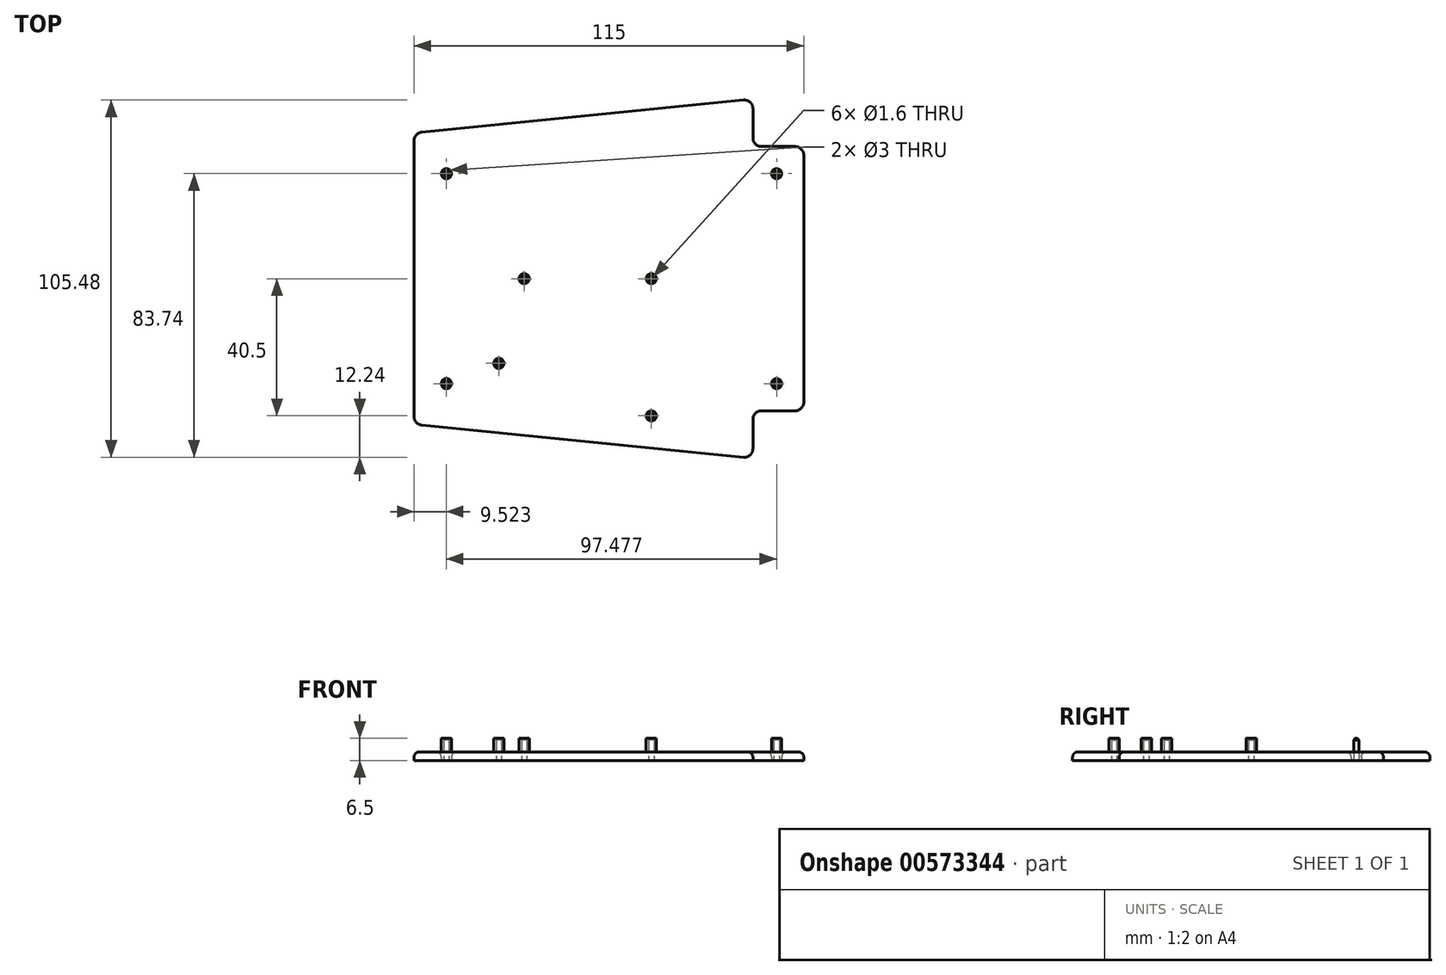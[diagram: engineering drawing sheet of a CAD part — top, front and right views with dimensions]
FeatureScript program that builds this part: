
annotation { "Feature Type Name" : "Feature", "Feature Type Description" : "" }
export const myFeature = defineFeature(function(context is Context, id is Id, definition is map)
    precondition{}
    {
        {
            var Q0;
            Q0=qCreatedBy(makeId("Top.planeOp"),FACE);
            var sketch = newSketch(context, id + "F0", { "sketchPlane" : qUnion([Q0])});
            skLineSegment(sketch, "E0", {"start": v(100, 0) * mm, "end": v(115, 0) * mm, "construction": true});
            skLineSegment(sketch, "E1", {"start": v(115, 0) * mm, "end": v(125, 0) * mm, "construction": true});
            skLineSegment(sketch, "E2", {"start": v(125, 0) * mm, "end": v(125, -55.5) * mm, "construction": true});
            skLineSegment(sketch, "E3.MirrorCS", {"start": v(125, 0) * mm, "end": v(125, 55.5) * mm, "construction": true});
            skLineSegment(sketch, "E4", {"start": v(100, 0) * mm, "end": v(100, -39) * mm, "construction": true});
            skLineSegment(sketch, "E5.MirrorCS", {"start": v(100, 0) * mm, "end": v(100, 39) * mm, "construction": true});
            skLineSegment(sketch, "E6", {"start": v(115, 0) * mm, "end": v(115, -39) * mm, "construction": true});
            skLineSegment(sketch, "E7.MirrorCS", {"start": v(115, 0) * mm, "end": v(115, 39) * mm, "construction": true});
            skLineSegment(sketch, "E8", {"start": v(100, 39) * mm, "end": v(115, 39) * mm});
            skLineSegment(sketch, "E9", {"start": v(115, 39) * mm, "end": v(115, -39) * mm});
            skLineSegment(sketch, "E10", {"start": v(115, -39) * mm, "end": v(100, -39) * mm});
            skLineSegment(sketch, "E11", {"start": v(0, 0) * mm, "end": v(70, 0) * mm, "construction": true});
            skLineSegment(sketch, "E12", {"start": v(70, 0) * mm, "end": v(100, 0) * mm, "construction": true});
            skLineSegment(sketch, "E13", {"start": v(0, 43) * mm, "end": v(0, -43) * mm});
            skPoint(sketch, "E14", {"position": v(0, 0) * mm});
            skLineSegment(sketch, "E15", {"start": v(0, 43) * mm, "end": v(125, 55.5) * mm, "construction": true});
            skLineSegment(sketch, "E16", {"start": v(0, -43) * mm, "end": v(125, -55.5) * mm, "construction": true});
            skLineSegment(sketch, "E17", {"start": v(0, 43) * mm, "end": v(100, 53) * mm});
            skLineSegment(sketch, "E18", {"start": v(100, 53) * mm, "end": v(100, 39) * mm});
            skLineSegment(sketch, "E19", {"start": v(0, -43) * mm, "end": v(100, -53) * mm});
            skLineSegment(sketch, "E20", {"start": v(100, -53) * mm, "end": v(100, -39) * mm});
            skLineSegment(sketch, "E21", {"start": v(70, -50) * mm, "end": v(70, -40.5) * mm, "construction": true});
            skLineSegment(sketch, "E22", {"start": v(0, 0) * mm, "end": v(25, 0) * mm, "construction": true});
            skLineSegment(sketch, "E23", {"start": v(25, 0) * mm, "end": v(25, -25) * mm, "construction": true});
            skLineSegment(sketch, "E24", {"start": v(115, -39) * mm, "end": v(115, -31) * mm, "construction": true});
            skLineSegment(sketch, "E25", {"start": v(115, -31) * mm, "end": v(107, -31) * mm, "construction": true});
            skLineSegment(sketch, "E26", {"start": v(107, -31) * mm, "end": v(9.52, -31) * mm, "construction": true});
            skCircle(sketch, "E27", {"center": v(107, -31) * mm, "radius": 0.8 * mm});
            skCircle(sketch, "E28", {"center": v(107, -31) * mm, "radius": 1.5 * mm});
            skCircle(sketch, "E29", {"center": v(9.52, -31) * mm, "radius": 0.8 * mm});
            skCircle(sketch, "E30", {"center": v(9.52, -31) * mm, "radius": 1.5 * mm});
            skCircle(sketch, "E31", {"center": v(70, 0) * mm, "radius": 0.8 * mm});
            skCircle(sketch, "E32", {"center": v(70, 0) * mm, "radius": 1.5 * mm});
            skCircle(sketch, "E33.MirrorC", {"center": v(107, 31) * mm, "radius": 0.8 * mm});
            skCircle(sketch, "E34.MirrorC", {"center": v(107, 31) * mm, "radius": 1.5 * mm});
            skCircle(sketch, "E35.MirrorC", {"center": v(9.52, 31) * mm, "radius": 0.8 * mm});
            skCircle(sketch, "E36.MirrorC", {"center": v(9.52, 31) * mm, "radius": 1.5 * mm});
            skCircle(sketch, "E37", {"center": v(70, -40.5) * mm, "radius": 0.8 * mm});
            skCircle(sketch, "E38", {"center": v(70, -40.5) * mm, "radius": 1.5 * mm});
            skCircle(sketch, "E39", {"center": v(25, -25) * mm, "radius": 0.8 * mm});
            skCircle(sketch, "E40", {"center": v(25, -25) * mm, "radius": 1.5 * mm});
            skLineSegment(sketch, "E41", {"start": v(9.52, 31) * mm, "end": v(9.52, 0) * mm, "construction": true});
            skLineSegment(sketch, "E42", {"start": v(9.52, 0) * mm, "end": v(32.48, 0) * mm, "construction": true});
            skCircle(sketch, "E43", {"center": v(32.48, 0) * mm, "radius": 0.8 * mm});
            skCircle(sketch, "E44", {"center": v(32.48, 0) * mm, "radius": 1.5 * mm});
            skSolve(sketch);
        }
        {
            var Q0;
            Q0 = qSketchRegion(id + "F0", true);
            var Q1;
            Q1=makeQuery(id+"F0.imprint","IMPRINT",FACE,{"disambiguationData":[TD([[makeQuery(id+"F0.imprint","IMPRINT",EDGE,{"derivedFrom":sQuery(id+"F0.wireOp",EDGE,"yP3IW7ik-inlI-UZb4-dCVX-bzyky39zJpdE")}),1.0]])]});
            var Q2;
            Q2=makeQuery(id+"F0.imprint","IMPRINT",FACE,{"disambiguationData":[TD([[makeQuery(id+"F0.imprint","IMPRINT",EDGE,{"derivedFrom":sQuery(id+"F0.wireOp",EDGE,"d3c2d1fd-962e-4d65-9ec7-34b7a0bd3f57")}),1.0]])]});
            var Q3;
            Q3=makeQuery(id+"F0.imprint","IMPRINT",FACE,{"disambiguationData":[TD([[makeQuery(id+"F0.imprint","IMPRINT",EDGE,{"derivedFrom":sQuery(id+"F0.wireOp",EDGE,"3b557636-d0a0-4f6c-8126-1294ea602e12.MirrorC")}),-1.0]])]});
            var Q4;
            Q4=makeQuery(id+"F0.imprint","IMPRINT",FACE,{"disambiguationData":[TD([[makeQuery(id+"F0.imprint","IMPRINT",EDGE,{"derivedFrom":sQuery(id+"F0.wireOp",EDGE,"a88917f8-b90f-4899-a085-096b975503a4.MirrorC")}),1.0]])]});
            var Q5;
            Q5=makeQuery(id+"F0.imprint","IMPRINT",FACE,{"disambiguationData":[TD([[makeQuery(id+"F0.imprint","IMPRINT",EDGE,{"derivedFrom":sQuery(id+"F0.wireOp",EDGE,"207ba64d-3068-436c-978a-4e265721a09c")}),1.0]])]});
            var Q6;
            Q6=makeQuery(id+"F0.imprint","IMPRINT",FACE,{"disambiguationData":[TD([[makeQuery(id+"F0.imprint","IMPRINT",EDGE,{"derivedFrom":sQuery(id+"F0.wireOp",EDGE,"1c9a65f7-0733-48cb-88e4-d0e1516edaf7.MirrorC")}),-1.0]])]});
            extrude(context, id + "F1", {"entities" : qUnion([Q0, Q1, Q2, Q3, Q4, Q5, Q6]), "depth" : 2.5 * mm, "offsetDistance" : 25 * mm});
        }
        {
            var Q0;
            Q0=makeQuery(id+"F1.opExtrude","SWEPT_EDGE",EDGE,{"disambiguationData":[OSD([sQuery(id+"F0.wireOp",EDGE,"E8"),sQuery(id+"F0.wireOp",EDGE,"E18")])]});
            var Q1;
            Q1=makeQuery(id+"F1.opExtrude","SWEPT_EDGE",EDGE,{"disambiguationData":[OSD([sQuery(id+"F0.wireOp",EDGE,"E17"),sQuery(id+"F0.wireOp",EDGE,"E18")])]});
            var Q2;
            Q2=makeQuery(id+"F1.opExtrude","SWEPT_EDGE",EDGE,{"disambiguationData":[OSD([sQuery(id+"F0.wireOp",EDGE,"E8"),sQuery(id+"F0.wireOp",EDGE,"E9")])]});
            var Q3;
            Q3=makeQuery(id+"F1.opExtrude","SWEPT_EDGE",EDGE,{"disambiguationData":[OSD([sQuery(id+"F0.wireOp",EDGE,"E13"),sQuery(id+"F0.wireOp",EDGE,"E17")])]});
            var Q4;
            Q4=makeQuery(id+"F1.opExtrude","SWEPT_EDGE",EDGE,{"disambiguationData":[OSD([sQuery(id+"F0.wireOp",EDGE,"E9"),sQuery(id+"F0.wireOp",EDGE,"E10")])]});
            var Q5;
            Q5=makeQuery(id+"F1.opExtrude","SWEPT_EDGE",EDGE,{"disambiguationData":[OSD([sQuery(id+"F0.wireOp",EDGE,"E10"),sQuery(id+"F0.wireOp",EDGE,"E20")])]});
            var Q6;
            Q6=makeQuery(id+"F1.opExtrude","SWEPT_EDGE",EDGE,{"disambiguationData":[OSD([sQuery(id+"F0.wireOp",EDGE,"E19"),sQuery(id+"F0.wireOp",EDGE,"E20")])]});
            var Q7;
            Q7=makeQuery(id+"F1.opExtrude","SWEPT_EDGE",EDGE,{"disambiguationData":[OSD([sQuery(id+"F0.wireOp",EDGE,"E13"),sQuery(id+"F0.wireOp",EDGE,"E19")])]});
            fillet(context, id + "F2", {"entities" : qUnion([Q0, Q1, Q2, Q3, Q4, Q5, Q6, Q7]), "radius" : 2.5 * mm, "tangentPropagation" : true, "allowEdgeOverflow" : false});
        }
        {
            var Q0;
            Q0=makeQuery(id+"F1.opExtrude","CAP_EDGE",EDGE,{"disambiguationData":[OSD([sQuery(id+"F0.wireOp",EDGE,"E13")])],"isStart":false});
            var Q1;
            Q1=makeQuery(id+"F1.opExtrude","CAP_EDGE",EDGE,{"disambiguationData":[OSD([sQuery(id+"F0.wireOp",EDGE,"E9")])],"isStart":false});
            var Q2;
            Q2=makeQuery(id+"F1.opExtrude","CAP_EDGE",EDGE,{"disambiguationData":[OSD([sQuery(id+"F0.wireOp",EDGE,"E17")])],"isStart":false});
            var Q3;
            Q3=makeQuery(id+"F1.opExtrude","CAP_EDGE",EDGE,{"disambiguationData":[OSD([sQuery(id+"F0.wireOp",EDGE,"E19")])],"isStart":false});
            var Q4;
            Q4=makeQuery(id+"F1.opExtrude","CAP_EDGE",EDGE,{"disambiguationData":[OSD([sQuery(id+"F0.wireOp",EDGE,"E20")])],"isStart":false});
            var Q5;
            Q5=makeQuery(id+"F1.opExtrude","CAP_EDGE",EDGE,{"disambiguationData":[OSD([sQuery(id+"F0.wireOp",EDGE,"E10")])],"isStart":false});
            var Q6;
            Q6=makeQuery(id+"F1.opExtrude","CAP_EDGE",EDGE,{"disambiguationData":[OSD([sQuery(id+"F0.wireOp",EDGE,"E8")])],"isStart":false});
            var Q7;
            Q7=makeQuery(id+"F1.opExtrude","CAP_EDGE",EDGE,{"disambiguationData":[OSD([sQuery(id+"F0.wireOp",EDGE,"E18")])],"isStart":false});
            fillet(context, id + "F3", {"entities" : qUnion([Q0, Q1, Q2, Q3, Q4, Q5, Q6, Q7]), "radius" : 1.5 * mm, "tangentPropagation" : true, "allowEdgeOverflow" : false});
        }
        {
            var Q0;
            Q0=makeQuery(id+"F0.imprint","IMPRINT",FACE,{"disambiguationData":[TD([[makeQuery(id+"F0.imprint","IMPRINT",EDGE,{"derivedFrom":sQuery(id+"F0.wireOp",EDGE,"E33.MirrorC")}),1.0]])]});
            var Q1;
            Q1=makeQuery(id+"F0.imprint","IMPRINT",FACE,{"disambiguationData":[TD([[makeQuery(id+"F0.imprint","IMPRINT",EDGE,{"derivedFrom":sQuery(id+"F0.wireOp",EDGE,"E31")}),-1.0]])]});
            var Q2;
            Q2=makeQuery(id+"F0.imprint","IMPRINT",FACE,{"disambiguationData":[TD([[makeQuery(id+"F0.imprint","IMPRINT",EDGE,{"derivedFrom":sQuery(id+"F0.wireOp",EDGE,"E27")}),-1.0]])]});
            var Q3;
            Q3=makeQuery(id+"F0.imprint","IMPRINT",FACE,{"disambiguationData":[TD([[makeQuery(id+"F0.imprint","IMPRINT",EDGE,{"derivedFrom":sQuery(id+"F0.wireOp",EDGE,"E37")}),-1.0]])]});
            var Q4;
            Q4=makeQuery(id+"F0.imprint","IMPRINT",FACE,{"disambiguationData":[TD([[makeQuery(id+"F0.imprint","IMPRINT",EDGE,{"derivedFrom":sQuery(id+"F0.wireOp",EDGE,"E39")}),-1.0]])]});
            var Q5;
            Q5=makeQuery(id+"F0.imprint","IMPRINT",FACE,{"disambiguationData":[TD([[makeQuery(id+"F0.imprint","IMPRINT",EDGE,{"derivedFrom":sQuery(id+"F0.wireOp",EDGE,"E29")}),-1.0]])]});
            var Q6;
            Q6=makeQuery(id+"F0.imprint","IMPRINT",FACE,{"disambiguationData":[TD([[makeQuery(id+"F0.imprint","IMPRINT",EDGE,{"derivedFrom":sQuery(id+"F0.wireOp",EDGE,"E35.MirrorC")}),1.0]])]});
            var Q7;
            Q7=makeQuery(id+"F0.imprint","IMPRINT",FACE,{"disambiguationData":[TD([[makeQuery(id+"F0.imprint","IMPRINT",EDGE,{"derivedFrom":sQuery(id+"F0.wireOp",EDGE,"XsraXnUc-tuvX-caLv-B0oX-IJHsb24Jevig")}),-1.0]])]});
            var Q8;
            Q8=makeQuery(id+"F0.imprint","IMPRINT",FACE,{"disambiguationData":[TD([[makeQuery(id+"F0.imprint","IMPRINT",EDGE,{"derivedFrom":sQuery(id+"F0.wireOp",EDGE,"E43")}),-1.0]])]});
            extrude(context, id + "F4", {"entities" : qUnion([Q0, Q1, Q2, Q3, Q4, Q5, Q6, Q7, Q8]), "operationType" : NewBodyOperationType.ADD, "depth" : 6.5 * mm, "offsetDistance" : 25 * mm});
        }
        {
            var Q0;
            Q0=makeQuery(id+"F1.opExtrude","CAP_EDGE",EDGE,{"disambiguationData":[OSD([sQuery(id+"F0.wireOp",EDGE,"E32")])],"isStart":false});
            var Q1;
            Q1=makeQuery(id+"F1.opExtrude","CAP_EDGE",EDGE,{"disambiguationData":[OSD([sQuery(id+"F0.wireOp",EDGE,"E40")])],"isStart":false});
            var Q2;
            Q2=makeQuery(id+"F1.opExtrude","CAP_EDGE",EDGE,{"disambiguationData":[OSD([sQuery(id+"F0.wireOp",EDGE,"E30")])],"isStart":false});
            var Q3;
            Q3=makeQuery(id+"F1.opExtrude","CAP_EDGE",EDGE,{"disambiguationData":[OSD([sQuery(id+"F0.wireOp",EDGE,"E36.MirrorC")])],"isStart":false});
            var Q4;
            Q4=makeQuery(id+"F1.opExtrude","CAP_EDGE",EDGE,{"disambiguationData":[OSD([sQuery(id+"F0.wireOp",EDGE,"E38")])],"isStart":false});
            var Q5;
            Q5=makeQuery(id+"F1.opExtrude","CAP_EDGE",EDGE,{"disambiguationData":[OSD([sQuery(id+"F0.wireOp",EDGE,"E28")])],"isStart":false});
            var Q6;
            Q6=makeQuery(id+"F1.opExtrude","CAP_EDGE",EDGE,{"disambiguationData":[OSD([sQuery(id+"F0.wireOp",EDGE,"E34.MirrorC")])],"isStart":false});
            var Q7;
            Q7=makeQuery(id+"F1.opExtrude","CAP_EDGE",EDGE,{"disambiguationData":[OSD([sQuery(id+"F0.wireOp",EDGE,"yHkl7EiW-Kaca-wJp6-ESLd-2S0sqFYlmHgj")])],"isStart":false});
            var Q8;
            Q8=makeQuery(id+"F1.opExtrude","CAP_EDGE",EDGE,{"disambiguationData":[OSD([sQuery(id+"F0.wireOp",EDGE,"E44")])],"isStart":false});
            fillet(context, id + "F5", {"entities" : qUnion([Q0, Q1, Q2, Q3, Q4, Q5, Q6, Q7, Q8]), "radius" : 1.5 * mm, "tangentPropagation" : true, "allowEdgeOverflow" : false});
        }
        {
            var Q0;
            Q0=makeQuery(id+"F4.opExtrude","CAP_EDGE",EDGE,{"disambiguationData":[OSD([sQuery(id+"F0.wireOp",EDGE,"E33.MirrorC")])],"isStart":false});
            var Q1;
            Q1=makeQuery(id+"F4.opExtrude","CAP_EDGE",EDGE,{"disambiguationData":[OSD([sQuery(id+"F0.wireOp",EDGE,"E27")])],"isStart":false});
            var Q2;
            Q2=makeQuery(id+"F4.opExtrude","CAP_EDGE",EDGE,{"disambiguationData":[OSD([sQuery(id+"F0.wireOp",EDGE,"E37")])],"isStart":false});
            var Q3;
            Q3=makeQuery(id+"F4.opExtrude","CAP_EDGE",EDGE,{"disambiguationData":[OSD([sQuery(id+"F0.wireOp",EDGE,"E31")])],"isStart":false});
            var Q4;
            Q4=makeQuery(id+"F4.opExtrude","CAP_EDGE",EDGE,{"disambiguationData":[OSD([sQuery(id+"F0.wireOp",EDGE,"E35.MirrorC")])],"isStart":false});
            var Q5;
            Q5=makeQuery(id+"F4.opExtrude","CAP_EDGE",EDGE,{"disambiguationData":[OSD([sQuery(id+"F0.wireOp",EDGE,"E39")])],"isStart":false});
            var Q6;
            Q6=makeQuery(id+"F4.opExtrude","CAP_EDGE",EDGE,{"disambiguationData":[OSD([sQuery(id+"F0.wireOp",EDGE,"E29")])],"isStart":false});
            var Q7;
            Q7=makeQuery(id+"F4.opExtrude","CAP_EDGE",EDGE,{"disambiguationData":[OSD([sQuery(id+"F0.wireOp",EDGE,"XsraXnUc-tuvX-caLv-B0oX-IJHsb24Jevig")])],"isStart":false});
            var Q8;
            Q8=makeQuery(id+"F4.opExtrude","CAP_EDGE",EDGE,{"disambiguationData":[OSD([sQuery(id+"F0.wireOp",EDGE,"E43")])],"isStart":false});
            chamfer(context, id + "F6", {"entities" : qUnion([Q0, Q1, Q2, Q3, Q4, Q5, Q6, Q7, Q8]), "width" : .5 * mm, "tangentPropagation" : true});
        }
    });
